# Revit family: Hand_Shower-Grohe-Euphoria_Cube+_26867_Series
name_source: partatom
category: Plumbing Fixtures
units: mm (PartAtom-declared; Revit-internal decimal feet)

## family parameters
Always vertical = No
Cut with Voids When Loaded = No
OmniClass Number = 23.45.05.14.17
OmniClass Title = Showers
Part Type = Normal
Room Calculation Point = No
Round Connector Dimension = Use Diameter
Shared = Yes
Work Plane-Based = Yes

## types (5) — shared parameters
Assembly Code = D2010710
CEC Compliant = Yes
CW Connection = No
CWFU = 3
CalGreen Compliant = Yes
Default Elevation = 0"
Description = Euphoria Cube+ Stick Hand Shower- 1 Spray
Flow Rate = 1.75 gpm (6.6 l/min)
HW Connection = No
HWFU = 3
IAPMO Compliance = • Massachusetts Plumbing Board Approved  • CSA B125.1 • ASME A112.18.1
Length = 8 1/2"
Manufacturer = Grohe
Orifice Material = Rubber-Grohe-White
Price = Prices may vary. Please consult Manufacturer Representative for most up-to-date price list.
Product Documentation Link = https://lixil.cdn.celum.cloud
Product Page URL = https://www.grohe.us
Tempered Water Connection = Yes
Tempered Water Connection Diameter = 1/2"
URL = https://www.grohe.us
Vent Connection = No
WFU = 4
Waste Connection = No
WaterSense = Yes
Width = 15/16"

## per-type parameters (varying)
| type | Finish | Material |
| 26867000 | Metal-Grohe-000-StarLight Chrome | Metal-Grohe-000-StarLight Chrome |
| 26867EN0 | Metal-Grohe-EN0-Brushed Nickel Infinity Finish | Metal-Grohe-EN0-Brushed Nickel Infinity Finish |
| 26867GN0 | Metal-Grohe-GN0-Brushed Cool Sunrise | Metal-Grohe-GN0-Brushed Cool Sunrise |
| 26867A00 | Metal-Grohe-A00-Hard Graphite | Metal-Grohe-A00-Hard Graphite |
| 268672430 | Metal-Grohe-2430-Matte Black | Metal-Grohe-2430-Matte Black |

note: column(s) folded — value = type name in every type: Model

## geometry (parser evidence)
native form markers: Sweep x2
no freeform markers — native parametric forms only
